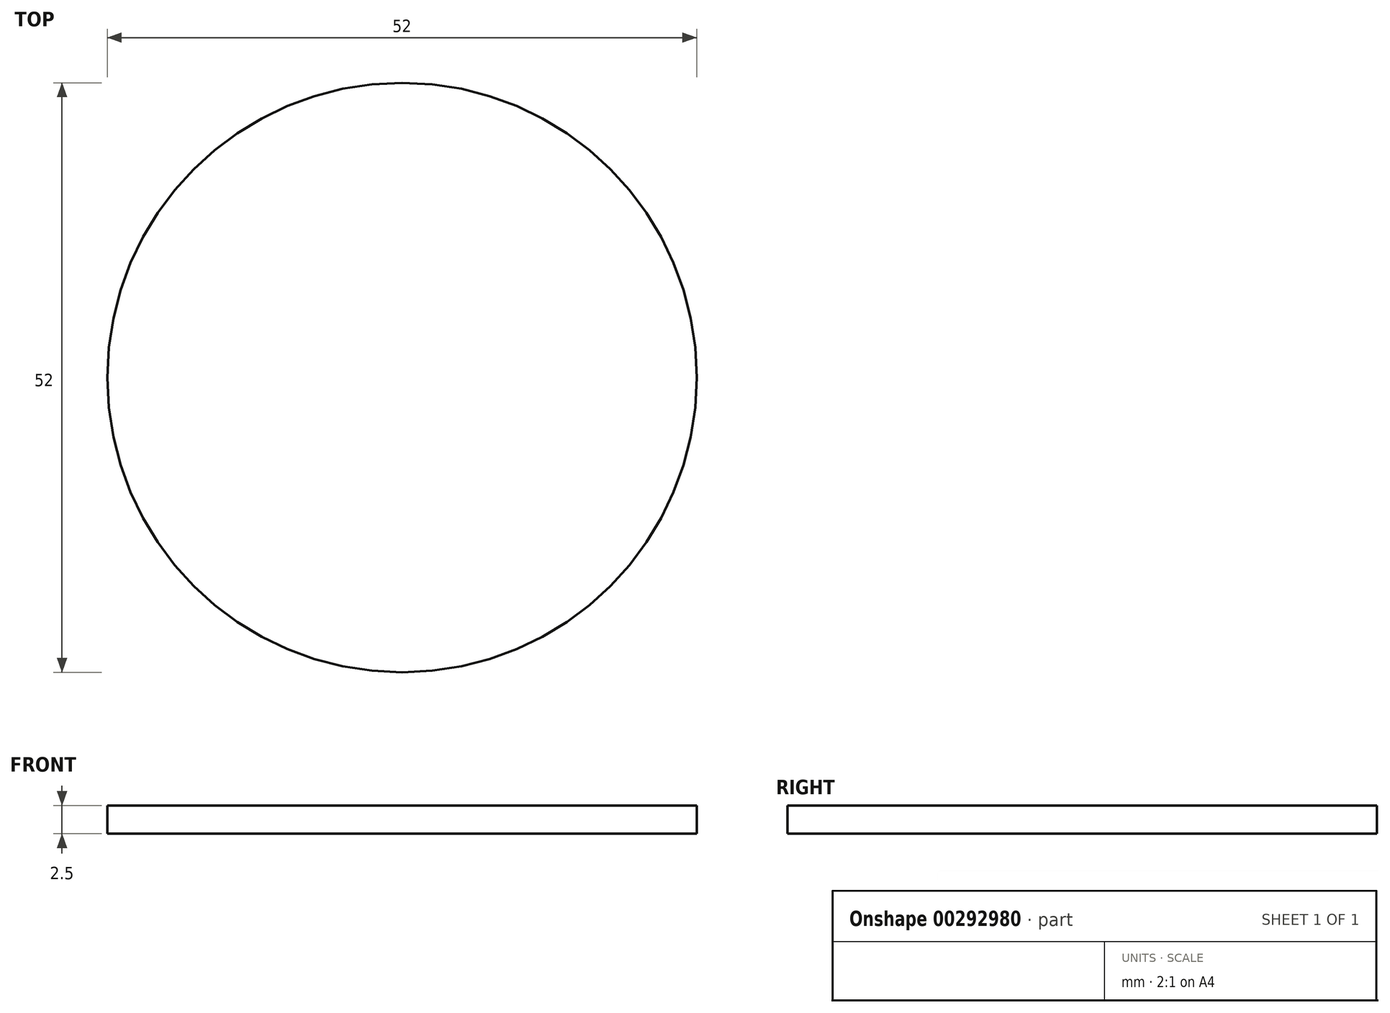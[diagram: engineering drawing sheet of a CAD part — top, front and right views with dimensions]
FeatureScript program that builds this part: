
annotation { "Feature Type Name" : "Feature", "Feature Type Description" : "" }
export const myFeature = defineFeature(function(context is Context, id is Id, definition is map)
    precondition{}
    {
        {
            var Q0;
            Q0=qCreatedBy(makeId("Top.planeOp"),FACE);
            var sketch = newSketch(context, id + "F0", { "sketchPlane" : qUnion([Q0])});
            skCircle(sketch, "E0", {"center": v(0, 0) * mm, "radius": 26 * mm});
            skSolve(sketch);
        }
        {
            var Q0;
            Q0=makeQuery(id+"F0.imprint","IMPRINT",FACE,{"disambiguationData":[TD([[makeQuery(id+"F0.imprint","IMPRINT",EDGE,{"derivedFrom":sQuery(id+"F0.wireOp",EDGE,"E0")}),1.0]])]});
            extrude(context, id + "F1", {"entities" : qUnion([Q0]), "depth" : 2.5 * mm});
        }
    });
